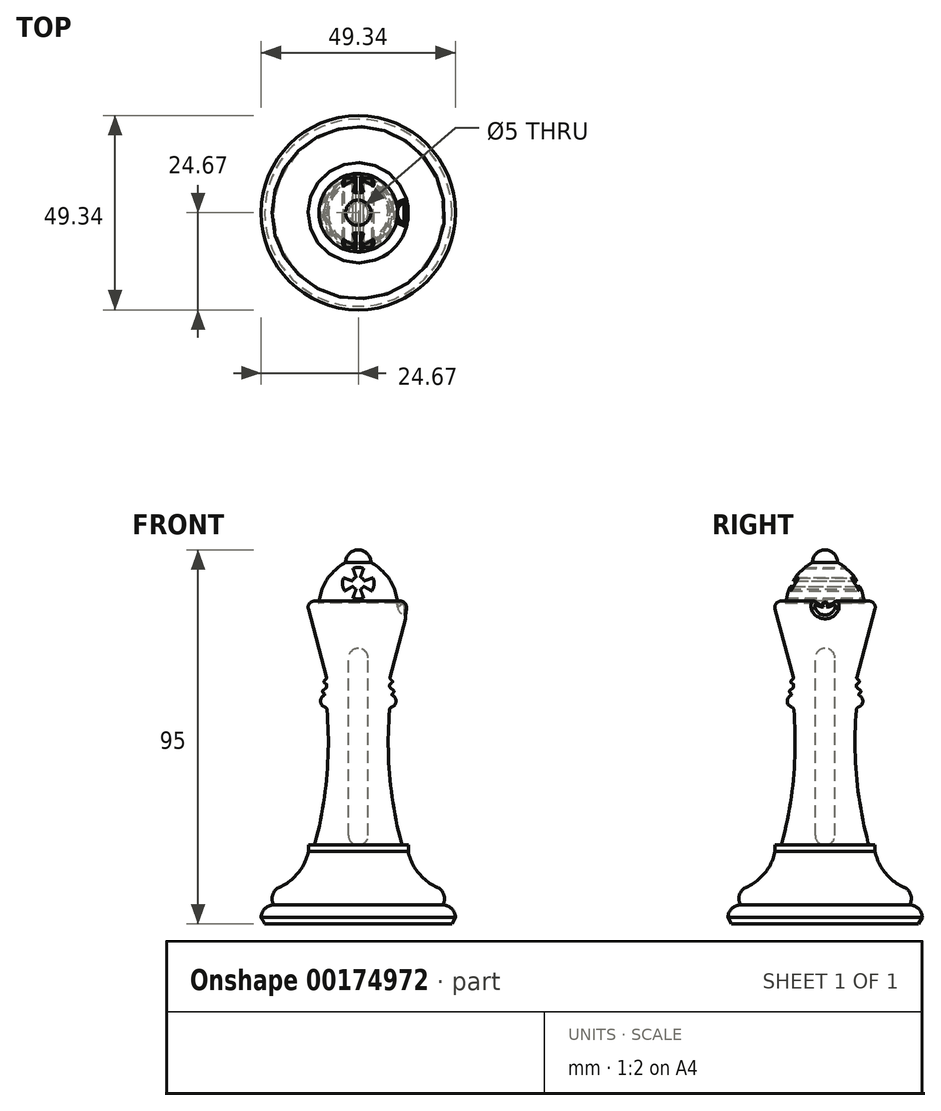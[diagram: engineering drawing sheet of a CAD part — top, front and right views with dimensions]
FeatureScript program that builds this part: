
annotation { "Feature Type Name" : "Feature", "Feature Type Description" : "" }
export const myFeature = defineFeature(function(context is Context, id is Id, definition is map)
    precondition{}
    {
        {
            var Q0;
            Q0=qCreatedBy(makeId("Front.planeOp"),FACE);
            var sketch = newSketch(context, id + "F0", { "sketchPlane" : qUnion([Q0])});
            skLineSegment(sketch, "E0", {"start": v(0, 0) * mm, "end": v(23.75, 0) * mm});
            skLineSegment(sketch, "E1", {"start": v(0, 0) * mm, "end": v(0, 95) * mm, "construction": true});
            skLineSegment(sketch, "E2", {"start": v(0, 20) * mm, "end": v(12.7, 20) * mm, "construction": true});
            skLineSegment(sketch, "E3", {"start": v(14.4, 55) * mm, "end": v(0, 55) * mm, "construction": true});
            skLineSegment(sketch, "E4", {"start": v(0, 80) * mm, "end": v(12.7, 80) * mm, "construction": true});
            skLineSegment(sketch, "E5", {"start": v(0, 64.34) * mm, "end": v(14.8, 64.34) * mm, "construction": true});
            skLineSegment(sketch, "E6", {"start": v(23.75, 0) * mm, "end": v(24.67, 1.6) * mm});
            skArc(sketch, "E7", {"start": v(24.67, 1.6) * mm, "mid": v(23.74, 3.86) * mm, "end": v(21.47, 4.8) * mm});
            skLineSegment(sketch, "E8", {"start": v(12.7, 20) * mm, "end": v(12.7, 18.42) * mm});
            skArc(sketch, "E9", {"start": v(12.7, 18.42) * mm, "mid": v(15.24, 12.99) * mm, "end": v(20, 9.33) * mm});
            skArc(sketch, "E10", {"start": v(21.47, 4.8) * mm, "mid": v(21.75, 7.4) * mm, "end": v(20, 9.33) * mm});
            skLineSegment(sketch, "E11", {"start": v(12.7, 20) * mm, "end": v(11.1, 20) * mm});
            skArc(sketch, "E12", {"start": v(8, 55) * mm, "mid": v(8, 37.36) * mm, "end": v(11.1, 20) * mm});
            skLineSegment(sketch, "E13", {"start": v(12.7, 80) * mm, "end": v(8, 62.46) * mm});
            skArc(sketch, "E14", {"start": v(8, 55) * mm, "mid": v(9.59, 56.4) * mm, "end": v(8.4, 58.15) * mm});
            skLineSegment(sketch, "E15", {"start": v(8.4, 58.15) * mm, "end": v(9.2, 59.1) * mm});
            skLineSegment(sketch, "E16", {"start": v(9.2, 59.1) * mm, "end": v(8, 60.1) * mm});
            skLineSegment(sketch, "E17", {"start": v(8, 60.1) * mm, "end": v(8, 60.83) * mm});
            skLineSegment(sketch, "E18", {"start": v(8, 60.83) * mm, "end": v(8.8, 61.5) * mm});
            skLineSegment(sketch, "E19", {"start": v(8.8, 61.5) * mm, "end": v(8, 62.46) * mm});
            skLineSegment(sketch, "E20", {"start": v(4.03, 86) * mm, "end": v(0, 86) * mm, "construction": true});
            skLineSegment(sketch, "E21", {"start": v(0, 86) * mm, "end": v(0, 0) * mm});
            skLineSegment(sketch, "E22", {"start": v(0, 95) * mm, "end": v(0, 86) * mm});
            skArc(sketch, "E23", {"start": v(12.7, 80) * mm, "mid": v(12.06, 81.73) * mm, "end": v(10.22, 81.71) * mm});
            skArc(sketch, "E24", {"start": v(4.03, 86) * mm, "mid": v(5.62, 81.68) * mm, "end": v(10.22, 81.71) * mm});
            skLineSegment(sketch, "E25", {"start": v(4.03, 86) * mm, "end": v(0, 86) * mm});
            skSolve(sketch);
        }
        {
            var Q0;
            Q0 = qSketchRegion(id + "F0", true);
            var Q1;
            Q1=sQuery(id+"F0.wireOp",EDGE,"E1");
            revolve(context, id + "F1", {"entities" : qUnion([Q0]), "axis" : qUnion([Q1]), "revolveType" : RevolveType.FULL});
        }
        {
            var Q0;
            Q0=makeQuery(id+"F1.opRevolve","SWEPT_EDGE",EDGE,{"disambiguationData":[OSD([sQuery(id+"F0.wireOp",EDGE,"E12"),sQuery(id+"F0.wireOp",EDGE,"E14")])]});
            var Q1;
            Q1=makeQuery(id+"F1.opRevolve","SWEPT_EDGE",EDGE,{"disambiguationData":[OSD([sQuery(id+"F0.wireOp",EDGE,"E11"),sQuery(id+"F0.wireOp",EDGE,"E12")])]});
            fillet(context, id + "F2", {"entities" : qUnion([Q0, Q1]), "radius" : .8 * mm, "tangentPropagation" : true, "allowEdgeOverflow" : false});
        }
        {
            var Q0;
            Q0=makeQuery(id+"F1.opRevolve","SWEPT_EDGE",EDGE,{"disambiguationData":[OSD([sQuery(id+"F0.wireOp",EDGE,"E18"),sQuery(id+"F0.wireOp",EDGE,"E19")])]});
            var Q1;
            Q1=makeQuery(id+"F1.opRevolve","SWEPT_EDGE",EDGE,{"disambiguationData":[OSD([sQuery(id+"F0.wireOp",EDGE,"E15"),sQuery(id+"F0.wireOp",EDGE,"E16")])]});
            var Q2;
            Q2=makeQuery(id+"F1.opRevolve","SWEPT_EDGE",EDGE,{"disambiguationData":[OSD([sQuery(id+"F0.wireOp",EDGE,"E13"),sQuery(id+"F0.wireOp",EDGE,"E19")])]});
            var Q3;
            Q3=makeQuery(id+"F1.opRevolve","SWEPT_EDGE",EDGE,{"disambiguationData":[OSD([sQuery(id+"F0.wireOp",EDGE,"E17"),sQuery(id+"F0.wireOp",EDGE,"E18")])]});
            var Q4;
            Q4=makeQuery(id+"F1.opRevolve","SWEPT_EDGE",EDGE,{"disambiguationData":[OSD([sQuery(id+"F0.wireOp",EDGE,"E16"),sQuery(id+"F0.wireOp",EDGE,"E17")])]});
            var Q5;
            Q5=makeQuery(id+"F1.opRevolve","SWEPT_EDGE",EDGE,{"disambiguationData":[OSD([sQuery(id+"F0.wireOp",EDGE,"E14"),sQuery(id+"F0.wireOp",EDGE,"E15")])]});
            fillet(context, id + "F3", {"entities" : qUnion([Q0, Q1, Q2, Q3, Q4, Q5]), "radius" : .2 * mm, "tangentPropagation" : true, "allowEdgeOverflow" : false});
        }
        {
            var Q0;
            Q0=qCreatedBy(makeId("Front.planeOp"),FACE);
            var sketch = newSketch(context, id + "F4", { "sketchPlane" : qUnion([Q0])});
            skLineSegment(sketch, "E26.bottom", {"start": v(0, 20) * mm, "end": v(0, 20) * mm});
            skLineSegment(sketch, "E26.top", {"start": v(0, 70) * mm, "end": v(0, 70) * mm});
            skLineSegment(sketch, "E26.left", {"start": v(2.5, 22.5) * mm, "end": v(2.5, 67.5) * mm});
            skPoint(sketch, "E26.middle", {"position": v(0, 45) * mm});
            skPoint(sketch, "E27.visualSharp", {"position": v(2.5, 70) * mm});
            skArc(sketch, "E27.filletArc", {"start": v(2.5, 67.5) * mm, "mid": v(1.77, 69.27) * mm, "end": v(0, 70) * mm});
            skPoint(sketch, "E28.visualSharp", {"position": v(-2.5, 70) * mm});
            skPoint(sketch, "E29.visualSharp", {"position": v(-2.5, 20) * mm});
            skPoint(sketch, "E30.visualSharp", {"position": v(2.5, 20) * mm});
            skArc(sketch, "E30.filletArc", {"start": v(0, 20) * mm, "mid": v(1.77, 20.73) * mm, "end": v(2.5, 22.5) * mm});
            skLineSegment(sketch, "E31", {"start": v(0, 70) * mm, "end": v(0, 20) * mm});
            skSolve(sketch);
        }
        {
            var Q0;
            Q0 = qSketchRegion(id + "F4", true);
            var Q1;
            Q1 = qConstructionFilter(qBodyType(qCreatedBy(id + "F4" ,EDGE), BodyType.WIRE), ConstructionObject.NO);
            var Q2;
            Q2=sQuery(id+"F4.wireOp",EDGE,"E31");
            revolve(context, id + "F5", {"operationType" : NewBodyOperationType.REMOVE, "entities" : qUnion([Q0]), "surfaceEntities" : qUnion([Q1]), "axis" : qUnion([Q2]), "revolveType" : RevolveType.FULL});
        }
        {
            var Q0;
            Q0=qCreatedBy(makeId("Front.planeOp"),FACE);
            var sketch = newSketch(context, id + "F6", { "sketchPlane" : qUnion([Q0])});
            skArc(sketch, "E32", {"start": v(3.2, 91.8) * mm, "mid": v(2.26, 94.06) * mm, "end": v(0, 95) * mm});
            skArc(sketch, "E33", {"start": v(10, 80) * mm, "mid": v(8.32, 86.89) * mm, "end": v(3.2, 91.8) * mm});
            skLineSegment(sketch, "E34", {"start": v(0, 95) * mm, "end": v(0, 80) * mm});
            skLineSegment(sketch, "E35", {"start": v(0, 80) * mm, "end": v(10, 80) * mm});
            skSolve(sketch);
        }
        {
            var Q0;
            Q0 = qSketchRegion(id + "F6", true);
            var Q1;
            Q1=sQuery(id+"F6.wireOp",EDGE,"E34");
            revolve(context, id + "F7", {"operationType" : NewBodyOperationType.ADD, "entities" : qUnion([Q0]), "axis" : qUnion([Q1]), "revolveType" : RevolveType.FULL});
        }
        {
            var Q0;
            Q0=qCreatedBy(makeId("Front.planeOp"),FACE);
            var sketch = newSketch(context, id + "F8", { "sketchPlane" : qUnion([Q0])});
            skArc(sketch, "E36", {"start": v(12.7, 78.2) * mm, "mid": v(15.5, 81) * mm, "end": v(12.7, 83.8) * mm});
            skLineSegment(sketch, "E37", {"start": v(12.7, 83.8) * mm, "end": v(12.7, 78.2) * mm});
            skSolve(sketch);
        }
        {
            var Q0;
            Q0 = qSketchRegion(id + "F8", true);
            var Q1;
            Q1=sQuery(id+"F8.wireOp",EDGE,"E37");
            revolve(context, id + "F9", {"operationType" : NewBodyOperationType.REMOVE, "entities" : qUnion([Q0]), "axis" : qUnion([Q1]), "revolveType" : RevolveType.FULL, "oppositeDirection" : true});
        }
        {
            var Q0;
            Q0=makeQuery(id+"FpeIU6h96BVfR1p_1.1.F9.boolean.opBoolean","INTERSECT",EDGE,{"disambiguationData":[OD(0.0)],"derivedFrom":[makeQuery(id+"F1.opRevolve","SWEPT_FACE",FACE,{"disambiguationData":[OSD([sQuery(id+"F0.wireOp",EDGE,"E23")])]}),makeQuery(id+"FpeIU6h96BVfR1p_1.1.F9.opRevolve","SWEPT_FACE",FACE,{"disambiguationData":[OSD([sQuery(id+"F8.wireOp",EDGE,"E36")])]})]});
            var Q1;
            Q1=makeQuery(id+"FpeIU6h96BVfR1p_1.1.F9.boolean.opBoolean","INTERSECT",EDGE,{"disambiguationData":[OD(1.0)],"derivedFrom":[makeQuery(id+"F1.opRevolve","SWEPT_FACE",FACE,{"disambiguationData":[OSD([sQuery(id+"F0.wireOp",EDGE,"E23")])]}),makeQuery(id+"FpeIU6h96BVfR1p_1.1.F9.opRevolve","SWEPT_FACE",FACE,{"disambiguationData":[OSD([sQuery(id+"F8.wireOp",EDGE,"E36")])]})]});
            var Q2;
            Q2=makeQuery(id+"FpeIU6h96BVfR1p_1.2.F9.boolean.opBoolean","COPY",FACE,{"derivedFrom":makeQuery(id+"FpeIU6h96BVfR1p_1.2.F9.opRevolve","SWEPT_FACE",FACE,{"disambiguationData":[OSD([sQuery(id+"F8.wireOp",EDGE,"E36")])]})});
            var Q3;
            Q3=makeQuery(id+"FpeIU6h96BVfR1p_1.4.F9.boolean.opBoolean","COPY",FACE,{"derivedFrom":makeQuery(id+"FpeIU6h96BVfR1p_1.4.F9.opRevolve","SWEPT_FACE",FACE,{"disambiguationData":[OSD([sQuery(id+"F8.wireOp",EDGE,"E36")])]})});
            var Q4;
            Q4=makeQuery(id+"FpeIU6h96BVfR1p_1.3.F9.boolean.opBoolean","COPY",FACE,{"derivedFrom":makeQuery(id+"FpeIU6h96BVfR1p_1.3.F9.opRevolve","SWEPT_FACE",FACE,{"disambiguationData":[OSD([sQuery(id+"F8.wireOp",EDGE,"E36")])]})});
            var Q5;
            Q5=makeQuery(id+"FpeIU6h96BVfR1p_1.5.F9.boolean.opBoolean","COPY",FACE,{"derivedFrom":makeQuery(id+"FpeIU6h96BVfR1p_1.5.F9.opRevolve","SWEPT_FACE",FACE,{"disambiguationData":[OSD([sQuery(id+"F8.wireOp",EDGE,"E36")])]})});
            var Q6;
            Q6=makeQuery(id+"F9.boolean.opBoolean","COPY",FACE,{"derivedFrom":makeQuery(id+"F9.opRevolve","SWEPT_FACE",FACE,{"disambiguationData":[OSD([sQuery(id+"F8.wireOp",EDGE,"E36")])]})});
            var Q7;
            Q7=makeQuery(id+"FpeIU6h96BVfR1p_1.6.F9.boolean.opBoolean","COPY",FACE,{"derivedFrom":makeQuery(id+"FpeIU6h96BVfR1p_1.6.F9.opRevolve","SWEPT_FACE",FACE,{"disambiguationData":[OSD([sQuery(id+"F8.wireOp",EDGE,"E36")])]})});
            fillet(context, id + "F10", {"entities" : qUnion([Q0, Q1, Q2, Q3, Q4, Q5, Q6, Q7]), "radius" : .8 * mm, "tangentPropagation" : true, "allowEdgeOverflow" : false});
        }
        {
            var Q0;
            Q0=qCreatedBy(makeId("Front.planeOp"),FACE);
            var sketch = newSketch(context, id + "F11", { "sketchPlane" : qUnion([Q0])});
            skLineSegment(sketch, "E38", {"start": v(0, 54.04) * mm, "end": v(0, 82.14) * mm, "construction": true});
            skArc(sketch, "E39", {"start": v(-0.55, 88.06) * mm, "mid": v(-1.13, 87.69) * mm, "end": v(-1.5, 87.1) * mm});
            skArc(sketch, "E40", {"start": v(-3.76, 87.92) * mm, "mid": v(-3.98, 86.2) * mm, "end": v(-3.46, 84.56) * mm});
            skLineSegment(sketch, "E41", {"start": v(0, 86.56) * mm, "end": v(1.6, 86.56) * mm, "construction": true});
            skLineSegment(sketch, "E42", {"start": v(0, 86.56) * mm, "end": v(2.83, 89.38) * mm, "construction": true});
            skLineSegment(sketch, "E43", {"start": v(0.55, 88.06) * mm, "end": v(1.37, 90.32) * mm});
            skLineSegment(sketch, "E44", {"start": v(1.5, 87.1) * mm, "end": v(3.76, 87.92) * mm});
            skLineSegment(sketch, "E45", {"start": v(0.55, 85.05) * mm, "end": v(1.37, 82.8) * mm});
            skLineSegment(sketch, "E46", {"start": v(1.39, 85.76) * mm, "end": v(3.46, 84.56) * mm});
            skLineSegment(sketch, "E47.MirrorCS", {"start": v(-0.55, 85.05) * mm, "end": v(-1.37, 82.8) * mm});
            skLineSegment(sketch, "E48.MirrorCS", {"start": v(-1.39, 85.76) * mm, "end": v(-3.46, 84.56) * mm});
            skLineSegment(sketch, "E49.MirrorCS", {"start": v(-1.5, 87.1) * mm, "end": v(-3.76, 87.92) * mm});
            skLineSegment(sketch, "E50.MirrorCS", {"start": v(-0.55, 88.06) * mm, "end": v(-1.37, 90.32) * mm});
            skArc(sketch, "E51.trimOffspring", {"start": v(1.37, 90.32) * mm, "mid": v(0, 90.56) * mm, "end": v(-1.37, 90.32) * mm});
            skArc(sketch, "E52.trimOffspring", {"start": v(1.5, 87.1) * mm, "mid": v(1.13, 87.69) * mm, "end": v(0.55, 88.06) * mm});
            skArc(sketch, "E53.trimOffspring", {"start": v(3.46, 84.56) * mm, "mid": v(3.98, 86.2) * mm, "end": v(3.76, 87.92) * mm});
            skArc(sketch, "E54.trimOffspring", {"start": v(0.55, 85.05) * mm, "mid": v(1.03, 85.33) * mm, "end": v(1.39, 85.76) * mm});
            skArc(sketch, "E55.trimOffspring", {"start": v(-1.37, 82.8) * mm, "mid": v(0, 82.56) * mm, "end": v(1.37, 82.8) * mm});
            skArc(sketch, "E56.trimOffspring", {"start": v(-1.39, 85.76) * mm, "mid": v(-1.03, 85.33) * mm, "end": v(-0.55, 85.05) * mm});
            skSolve(sketch);
        }
        {
            var Q0;
            Q0 = qSketchRegion(id + "F11", true);
            extrude(context, id + "F12", {"entities" : qUnion([Q0]), "operationType" : NewBodyOperationType.REMOVE, "depth" : 25 * mm, "symmetric" : true});
        }
    });
